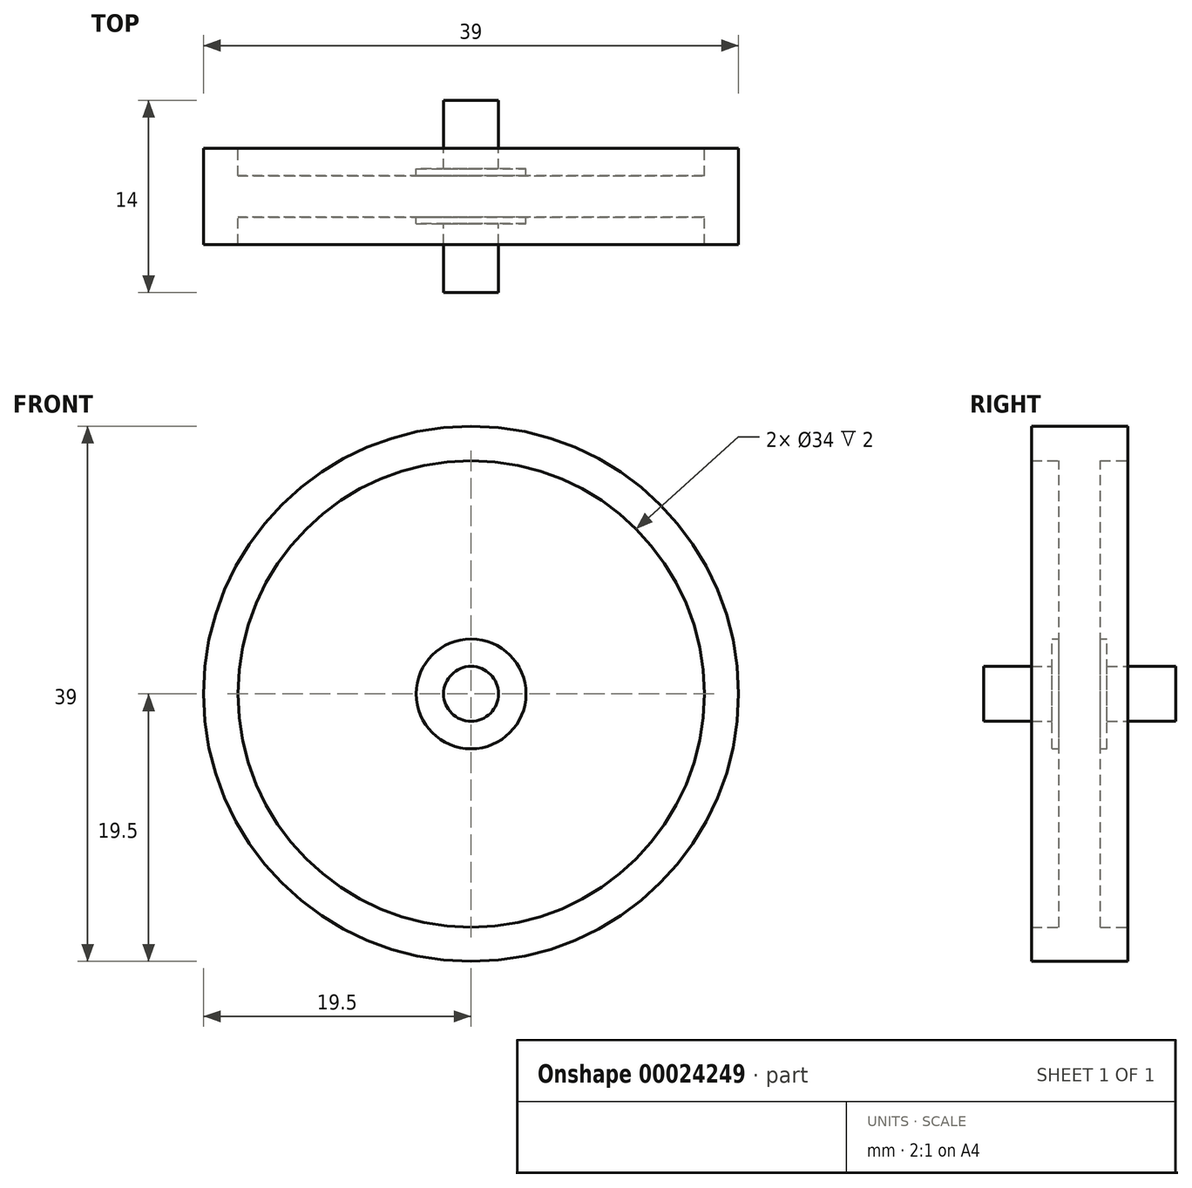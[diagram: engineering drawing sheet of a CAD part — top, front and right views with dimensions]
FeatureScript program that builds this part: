
annotation { "Feature Type Name" : "Feature", "Feature Type Description" : "" }
export const myFeature = defineFeature(function(context is Context, id is Id, definition is map)
    precondition{}
    {
        {
            var Q0;
            Q0=qCreatedBy(makeId("Front.planeOp"),FACE);
            var sketch = newSketch(context, id + "F0", { "sketchPlane" : qUnion([Q0])});
            skCircle(sketch, "E0", {"center": v(0, 0) * mm, "radius": 19.5 * mm});
            skCircle(sketch, "E1", {"center": v(0, 0) * mm, "radius": 2 * mm});
            skCircle(sketch, "E2", {"center": v(0, 0) * mm, "radius": 4 * mm});
            skCircle(sketch, "E3", {"center": v(0, 0) * mm, "radius": 17 * mm});
            skSolve(sketch);
        }
        {
            var Q0;
            Q0=makeQuery(id+"F0.imprint","IMPRINT",FACE,{"disambiguationData":[TD([[makeQuery(id+"F0.imprint","IMPRINT",EDGE,{"derivedFrom":sQuery(id+"F0.wireOp",EDGE,"E0")}),1.0]])]});
            extrude(context, id + "F1", {"entities" : qUnion([Q0]), "endBound" : BoundingType.SYMMETRIC, "depth" : 7 * mm});
        }
        {
            var Q0;
            Q0=makeQuery(id+"F0.imprint","IMPRINT",FACE,{"disambiguationData":[TD([[makeQuery(id+"F0.imprint","IMPRINT",EDGE,{"derivedFrom":sQuery(id+"F0.wireOp",EDGE,"E2")}),-1.0]])]});
            extrude(context, id + "F2", {"entities" : qUnion([Q0]), "operationType" : NewBodyOperationType.ADD, "endBound" : BoundingType.SYMMETRIC, "depth" : 3 * mm});
        }
        {
            var Q0;
            Q0=makeQuery(id+"F0.imprint","IMPRINT",FACE,{"disambiguationData":[TD([[makeQuery(id+"F0.imprint","IMPRINT",EDGE,{"derivedFrom":sQuery(id+"F0.wireOp",EDGE,"E1")}),-1.0]])]});
            extrude(context, id + "F3", {"entities" : qUnion([Q0]), "operationType" : NewBodyOperationType.ADD, "endBound" : BoundingType.SYMMETRIC, "depth" : 4 * mm});
        }
        {
            var Q0;
            Q0=makeQuery(id+"F0.imprint","IMPRINT",FACE,{"disambiguationData":[TD([[makeQuery(id+"F0.imprint","IMPRINT",EDGE,{"derivedFrom":sQuery(id+"F0.wireOp",EDGE,"E1")}),1.0]])]});
            extrude(context, id + "F4", {"entities" : qUnion([Q0]), "operationType" : NewBodyOperationType.ADD, "endBound" : BoundingType.SYMMETRIC, "depth" : 14 * mm});
        }
    });
